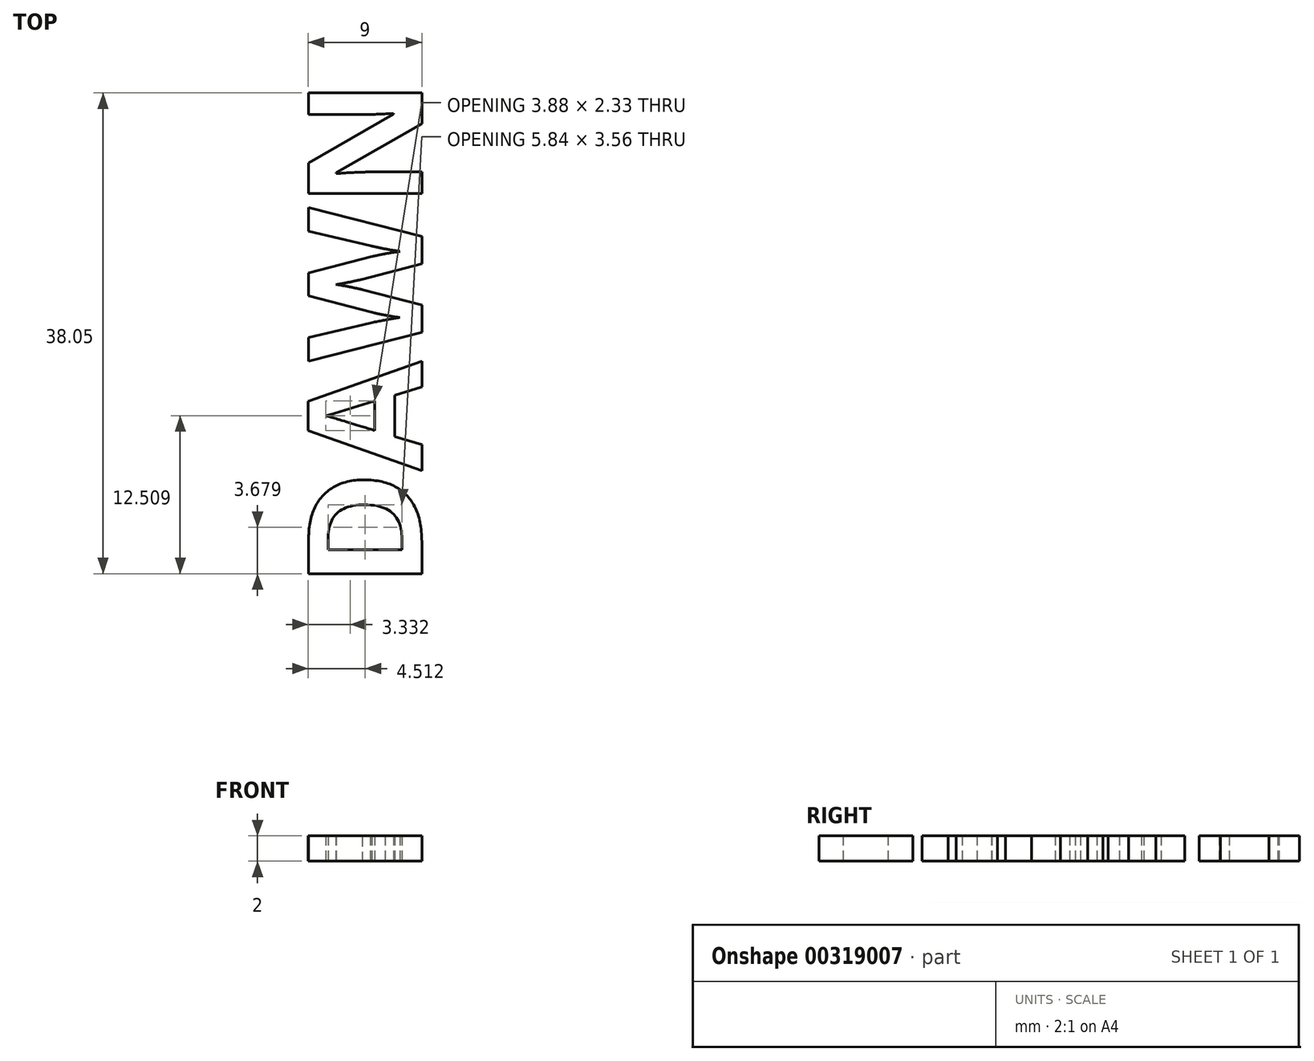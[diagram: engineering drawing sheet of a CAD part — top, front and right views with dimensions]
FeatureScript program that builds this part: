
annotation { "Feature Type Name" : "Feature", "Feature Type Description" : "" }
export const myFeature = defineFeature(function(context is Context, id is Id, definition is map)
    precondition{}
    {
        {
            var Q0;
            Q0=qCreatedBy(makeId("Top.planeOp"),FACE);
            var sketch = newSketch(context, id + "F0", { "sketchPlane" : qUnion([Q0])});
            skText(sketch, "E0", { "text": "DAWN", "fontName": "OpenSans-Bold.ttf"});
            const initialGuessF0  = {"E0": [0, 1e-05, 0, 1, 0.00904]};
            skSetInitialGuess(sketch, initialGuessF0);
            skSolve(sketch);
        }
        {
            var Q0;
            Q0 = qSketchRegion(id + "F0", true);
            extrude(context, id + "F1", {"entities" : qUnion([Q0]), "depth" : 2 * mm, "offsetDistance" : 25 * mm});
        }
    });
